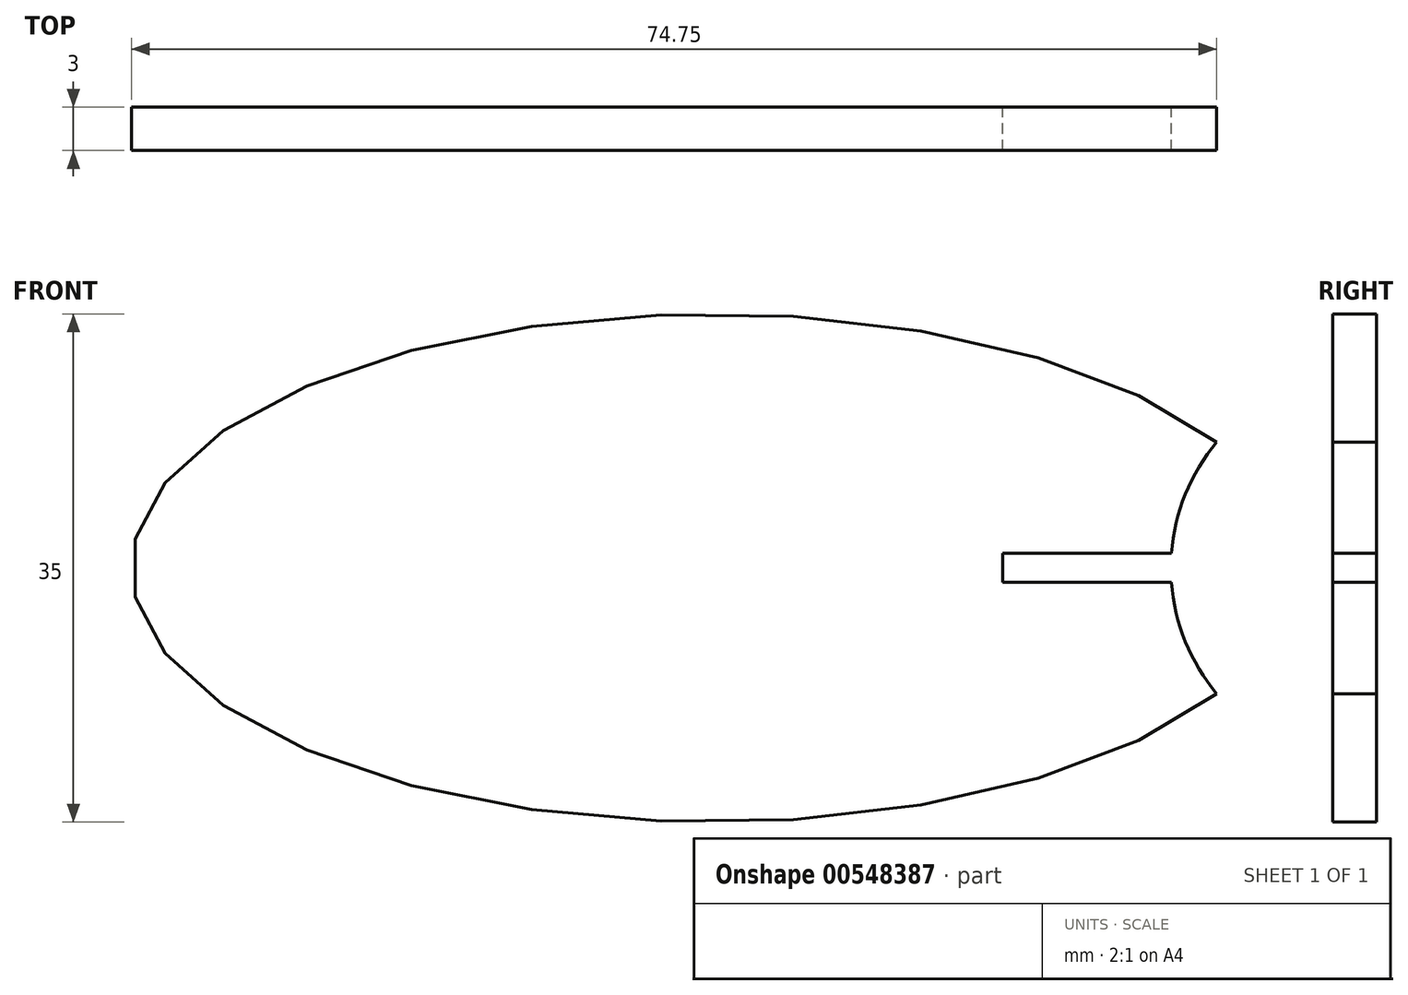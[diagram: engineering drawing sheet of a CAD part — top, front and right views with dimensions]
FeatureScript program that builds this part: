
annotation { "Feature Type Name" : "Feature", "Feature Type Description" : "" }
export const myFeature = defineFeature(function(context is Context, id is Id, definition is map)
    precondition{}
    {
        {
            var Q0;
            Q0=qCreatedBy(makeId("Front.planeOp"),FACE);
            var sketch = newSketch(context, id + "F0", { "sketchPlane" : qUnion([Q0])});
            skEllipse(sketch, "E0", {"center": v(0, 0) * mm, "majorRadius": 40 * mm, "minorRadius": 17.5 * mm, "majorAxis": v(-1, 0)});
            skSolve(sketch);
        }
        {
            var Q0;
            Q0=qSketchRegion(id+"F0",true);
            extrude(context, id + "F1", {"entities" : qUnion([Q0]), "depth" : 3 * mm});
        }
        {
            var Q0;
            Q0=qCreatedBy(makeId("Front.planeOp"),FACE);
            var sketch = newSketch(context, id + "F2", { "sketchPlane" : qUnion([Q0])});
            skCircle(sketch, "E1", {"center": v(45.1, 0) * mm, "radius": 13.5 * mm});
            skSolve(sketch);
        }
        {
            var Q0;
            Q0=qSketchRegion(id+"F2",true);
            extrude(context, id + "F3", {"entities" : qUnion([Q0]), "operationType" : NewBodyOperationType.REMOVE, "depth" : 25 * mm});
        }
        {
            var Q0;
            Q0=qCreatedBy(makeId("Front.planeOp"),FACE);
            var sketch = newSketch(context, id + "F4", { "sketchPlane" : qUnion([Q0])});
            skLineSegment(sketch, "E2.bottom", {"start": v(20, 1) * mm, "end": v(40, 1) * mm});
            skLineSegment(sketch, "E2.top", {"start": v(20, 0) * mm, "end": v(40, 0) * mm});
            skLineSegment(sketch, "E2.left", {"start": v(20, 1) * mm, "end": v(20, 0) * mm});
            skLineSegment(sketch, "E2.right", {"start": v(40, 1) * mm, "end": v(40, 0) * mm});
            skLineSegment(sketch, "E3.MirrorCS", {"start": v(20, -1) * mm, "end": v(40, -1) * mm});
            skLineSegment(sketch, "E4.MirrorCS", {"start": v(40, -1) * mm, "end": v(40, 0) * mm});
            skLineSegment(sketch, "E5.MirrorCS", {"start": v(20, -1) * mm, "end": v(20, 0) * mm});
            skSolve(sketch);
        }
        {
            var Q0;
            Q0=qSketchRegion(id+"F4",true);
            extrude(context, id + "F5", {"entities" : qUnion([Q0]), "operationType" : NewBodyOperationType.REMOVE, "depth" : 25 * mm});
        }
    });
